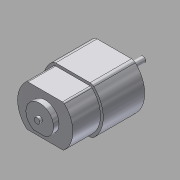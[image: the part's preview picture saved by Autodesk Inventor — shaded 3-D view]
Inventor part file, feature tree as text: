
AUTODESK INVENTOR PART (.ipt)
format: ipt  version: 2015 (Build 190159000, 159)  size: 155,648 bytes
history: native  units: mm
features: extrude x5, sketch x5, fillet x4
ambient origin geometry x8: Origin, YZ Plane, XZ Plane, XY Plane, X Axis, Y Axis, Z Axis, Center Point
bodies: Solid1 (feature_tree)
feature tree (14):
  extrude  "Extrusion1"  Depth=8.4mm TaperAngle=0.0deg
  extrude  "Extrusion2"  Depth=2.0mm TaperAngle=0.0deg
  extrude  "Extrusion3"  Depth=10.0mm
  extrude  "Extrusion4"  Depth=2.0mm
  extrude  "Extrusion5"  Depth=1.0mm
  fillet  "Fillet7"  Radius=1.0mm
  fillet  "Fillet8"  Radius=1.0mm
  fillet  "Fillet9"  Radius=1.0mm
  fillet  "Fillet10"  Radius=1.0mm
  sketch  "Sketch1"  dims[d0=2.0mm d1=8.4mm d2=0.0mm]
  sketch  "Sketch2"  dims[d3=6.0mm d4=2.0mm d5=0.0mm]
  sketch  "Sketch3"  dims[d8=25.0mm d9=0.0mm d10=10.0mm]
  sketch  "Sketch4"  dims[d12=2.0mm d13=0.0mm d14=2.0mm]
  sketch  "Sketch5"  dims[d15=1.0mm d16=0.0mm d23=20.0mm d24=1.0mm d25=1.0mm d26=1.0mm d27=1.0mm]
